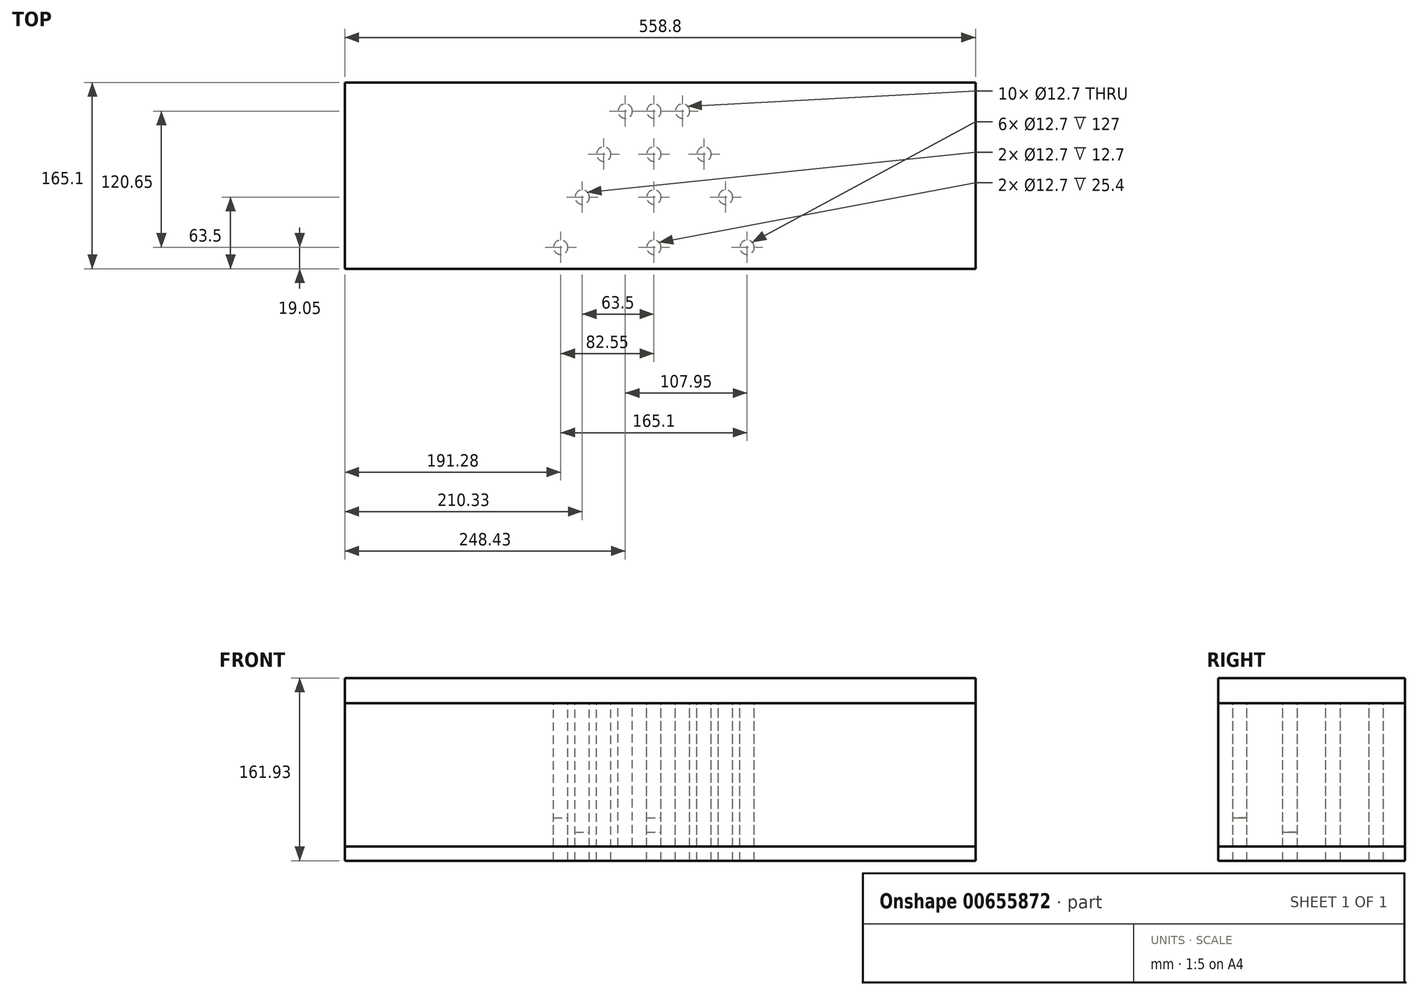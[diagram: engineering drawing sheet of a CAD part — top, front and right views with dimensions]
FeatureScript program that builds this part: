
annotation { "Feature Type Name" : "Feature", "Feature Type Description" : "" }
export const myFeature = defineFeature(function(context is Context, id is Id, definition is map)
    precondition{}
    {
        {
            var Q0;
            Q0=qCreatedBy(makeId("Top.planeOp"),FACE);
            var sketch = newSketch(context, id + "F0", { "sketchPlane" : qUnion([Q0])});
            skLineSegment(sketch, "E0.bottom", {"start": v(284.97, 82.55) * mm, "end": v(-273.83, 82.55) * mm});
            skLineSegment(sketch, "E0.top", {"start": v(284.97, -82.55) * mm, "end": v(-273.83, -82.55) * mm});
            skLineSegment(sketch, "E0.left", {"start": v(284.97, 82.55) * mm, "end": v(284.97, -82.55) * mm});
            skLineSegment(sketch, "E0.right", {"start": v(-273.83, 82.55) * mm, "end": v(-273.83, -82.55) * mm});
            skPoint(sketch, "E0.middle", {"position": v(5.57, 0) * mm});
            skSolve(sketch);
        }
        {
            var Q0;
            Q0 = qSketchRegion(id + "F0", true);
            extrude(context, id + "F1", {"entities" : qUnion([Q0]), "depth" : 22.22 * mm, "offsetDistance" : 25.4 * mm});
        }
        {
            var Q0;
            Q0=makeQuery(id+"F1.opExtrude","CAP_FACE",FACE,{"disambiguationData":[OSD([sQuery(id+"F0.wireOp",EDGE,"E0.bottom"),sQuery(id+"F0.wireOp",EDGE,"E0.top"),sQuery(id+"F0.wireOp",EDGE,"E0.left"),sQuery(id+"F0.wireOp",EDGE,"E0.right")])],"isStart":true});
            var sketch = newSketch(context, id + "F2", { "sketchPlane" : qUnion([Q0])});
            skLineSegment(sketch, "E1.0", {"start": v(284.97, 82.55) * mm, "end": v(-273.83, 82.55) * mm, "construction": true});
            skLineSegment(sketch, "E2.0", {"start": v(284.97, -82.55) * mm, "end": v(-273.83, -82.55) * mm, "construction": true});
            skLineSegment(sketch, "E3", {"start": v(0, 0) * mm, "end": v(0, 82.55) * mm, "construction": true});
            skLineSegment(sketch, "E4", {"start": v(0, 0) * mm, "end": v(0, -82.55) * mm, "construction": true});
            skCircle(sketch, "E5", {"center": v(-82.55, 63.5) * mm, "radius": 6.35 * mm});
            skCircle(sketch, "E6", {"center": v(-63.5, 19.05) * mm, "radius": 6.35 * mm});
            skCircle(sketch, "E7", {"center": v(-44.45, -19.05) * mm, "radius": 6.35 * mm});
            skCircle(sketch, "E8", {"center": v(-25.4, -57.15) * mm, "radius": 6.35 * mm});
            skCircle(sketch, "E9", {"center": v(0, 63.5) * mm, "radius": 6.35 * mm});
            skCircle(sketch, "E10", {"center": v(0, 19.05) * mm, "radius": 6.35 * mm});
            skCircle(sketch, "E11", {"center": v(0, -19.05) * mm, "radius": 6.35 * mm});
            skCircle(sketch, "E12", {"center": v(0, -57.15) * mm, "radius": 6.35 * mm});
            skCircle(sketch, "E13.MirrorC", {"center": v(63.5, 19.05) * mm, "radius": 6.35 * mm});
            skCircle(sketch, "E14.MirrorC", {"center": v(82.55, 63.5) * mm, "radius": 6.35 * mm});
            skCircle(sketch, "E15.MirrorC", {"center": v(44.45, -19.05) * mm, "radius": 6.35 * mm});
            skCircle(sketch, "E16.MirrorC", {"center": v(25.4, -57.15) * mm, "radius": 6.35 * mm});
            skSolve(sketch);
        }
        {
            var Q0;
            Q0=makeQuery(id+"F2.imprint","IMPRINT",FACE,{"disambiguationData":[TD([[makeQuery(id+"F2.imprint","IMPRINT",EDGE,{"derivedFrom":sQuery(id+"F2.wireOp",EDGE,"E5")}),1.0]])]});
            var Q1;
            Q1=makeQuery(id+"F2.imprint","IMPRINT",FACE,{"disambiguationData":[TD([[makeQuery(id+"F2.imprint","IMPRINT",EDGE,{"derivedFrom":sQuery(id+"F2.wireOp",EDGE,"E9")}),1.0]])]});
            var Q2;
            Q2=makeQuery(id+"F2.imprint","IMPRINT",FACE,{"disambiguationData":[TD([[makeQuery(id+"F2.imprint","IMPRINT",EDGE,{"derivedFrom":sQuery(id+"F2.wireOp",EDGE,"E14.MirrorC")}),-1.0]])]});
            extrude(context, id + "F3", {"entities" : qUnion([Q0, Q1, Q2]), "depth" : 101.6 * mm, "offsetDistance" : 25.4 * mm});
        }
        {
            var Q0;
            Q0=makeQuery(id+"F2.imprint","IMPRINT",FACE,{"disambiguationData":[TD([[makeQuery(id+"F2.imprint","IMPRINT",EDGE,{"derivedFrom":sQuery(id+"F2.wireOp",EDGE,"E6")}),1.0]])]});
            var Q1;
            Q1=makeQuery(id+"F2.imprint","IMPRINT",FACE,{"disambiguationData":[TD([[makeQuery(id+"F2.imprint","IMPRINT",EDGE,{"derivedFrom":sQuery(id+"F2.wireOp",EDGE,"E13.MirrorC")}),-1.0]])]});
            var Q2;
            Q2=makeQuery(id+"F2.imprint","IMPRINT",FACE,{"disambiguationData":[TD([[makeQuery(id+"F2.imprint","IMPRINT",EDGE,{"derivedFrom":sQuery(id+"F2.wireOp",EDGE,"E10")}),1.0]])]});
            extrude(context, id + "F4", {"entities" : qUnion([Q0, Q1, Q2]), "depth" : 114.3 * mm, "offsetDistance" : 25.4 * mm});
        }
        {
            var Q0;
            Q0=makeQuery(id+"F2.imprint","IMPRINT",FACE,{"disambiguationData":[TD([[makeQuery(id+"F2.imprint","IMPRINT",EDGE,{"derivedFrom":sQuery(id+"F2.wireOp",EDGE,"E7")}),1.0]])]});
            var Q1;
            Q1=makeQuery(id+"F2.imprint","IMPRINT",FACE,{"disambiguationData":[TD([[makeQuery(id+"F2.imprint","IMPRINT",EDGE,{"derivedFrom":sQuery(id+"F2.wireOp",EDGE,"E11")}),1.0]])]});
            var Q2;
            Q2=makeQuery(id+"F2.imprint","IMPRINT",FACE,{"disambiguationData":[TD([[makeQuery(id+"F2.imprint","IMPRINT",EDGE,{"derivedFrom":sQuery(id+"F2.wireOp",EDGE,"E15.MirrorC")}),-1.0]])]});
            extrude(context, id + "F5", {"entities" : qUnion([Q0, Q1, Q2]), "operationType" : NewBodyOperationType.ADD, "depth" : 127 * mm, "offsetDistance" : 25.4 * mm});
        }
        {
            var Q0;
            Q0=makeQuery(id+"F2.imprint","IMPRINT",FACE,{"disambiguationData":[TD([[makeQuery(id+"F2.imprint","IMPRINT",EDGE,{"derivedFrom":sQuery(id+"F2.wireOp",EDGE,"E16.MirrorC")}),-1.0]])]});
            var Q1;
            Q1=makeQuery(id+"F2.imprint","IMPRINT",FACE,{"disambiguationData":[TD([[makeQuery(id+"F2.imprint","IMPRINT",EDGE,{"derivedFrom":sQuery(id+"F2.wireOp",EDGE,"E12")}),1.0]])]});
            var Q2;
            Q2=makeQuery(id+"F2.imprint","IMPRINT",FACE,{"disambiguationData":[TD([[makeQuery(id+"F2.imprint","IMPRINT",EDGE,{"derivedFrom":sQuery(id+"F2.wireOp",EDGE,"E8")}),1.0]])]});
            var Q3;
            Q3=sQuery(id+"F2.wireOp",EDGE,"E16.MirrorC");
            var Q4;
            Q4=sQuery(id+"F2.wireOp",EDGE,"E12");
            var Q5;
            Q5=sQuery(id+"F2.wireOp",EDGE,"E8");
            extrude(context, id + "F6", {"entities" : qUnion([Q0, Q1, Q2]), "surfaceEntities" : qUnion([Q3, Q4, Q5]), "depth" : 139.7 * mm, "offsetDistance" : 25.4 * mm});
        }
    });
